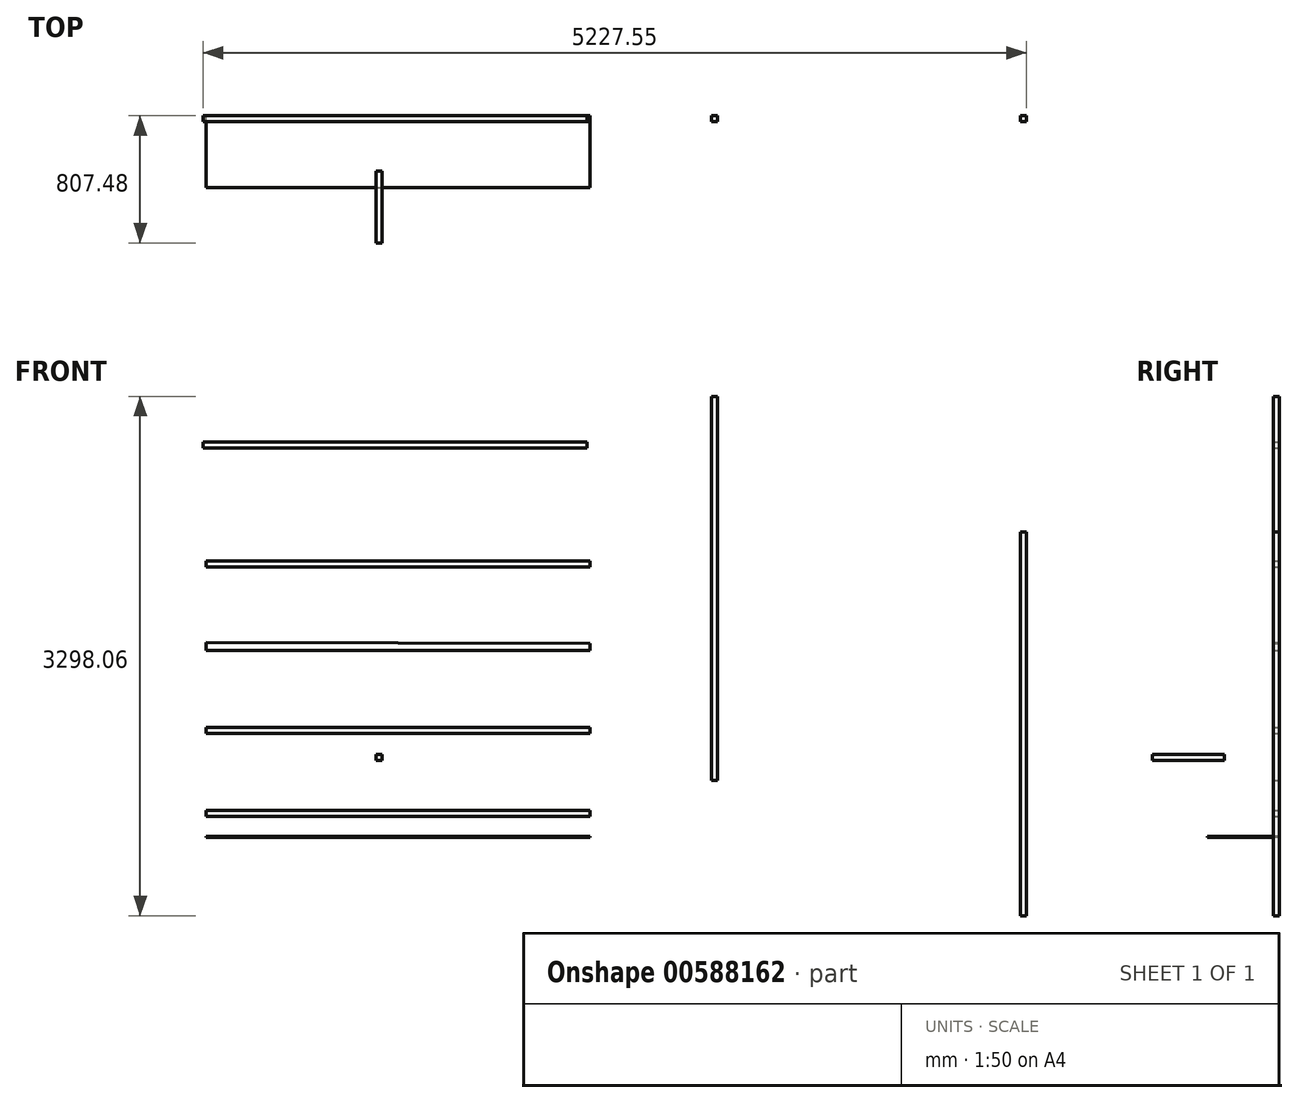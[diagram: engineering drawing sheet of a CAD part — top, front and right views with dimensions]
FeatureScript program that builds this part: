
annotation { "Feature Type Name" : "Feature", "Feature Type Description" : "" }
export const myFeature = defineFeature(function(context is Context, id is Id, definition is map)
    precondition{}
    {
        {
            var Q0;
            Q0=qCreatedBy(makeId("Front.planeOp"),FACE);
            var sketch = newSketch(context, id + "F0", { "sketchPlane" : qUnion([Q0])});
            skLineSegment(sketch, "E0", {"start": v(1359.2, 725.07) * mm, "end": v(1359.2, -1713.33) * mm});
            skLineSegment(sketch, "E1", {"start": v(-1079.2, 725.07) * mm, "end": v(-1079.2, -1713.33) * mm});
            skLineSegment(sketch, "E2", {"start": v(-1079.2, -525.88) * mm, "end": v(1359.2, -525.88) * mm});
            skLineSegment(sketch, "E3", {"start": v(-1079.2, -1052.93) * mm, "end": v(1359.2, -1052.93) * mm});
            skLineSegment(sketch, "E4.bottom", {"start": v(-1097.28, 798.65) * mm, "end": v(1341.12, 798.65) * mm});
            skLineSegment(sketch, "E4.top", {"start": v(-1097.28, 760.55) * mm, "end": v(1341.12, 760.55) * mm});
            skLineSegment(sketch, "E4.left", {"start": v(-1097.28, 798.65) * mm, "end": v(-1097.28, 760.55) * mm});
            skLineSegment(sketch, "E4.right", {"start": v(1341.12, 798.65) * mm, "end": v(1341.12, 760.55) * mm});
            skLineSegment(sketch, "E5.bottom", {"start": v(2131.45, 1087.28) * mm, "end": v(2169.55, 1087.28) * mm});
            skLineSegment(sketch, "E5.top", {"start": v(2131.45, -1351.12) * mm, "end": v(2169.55, -1351.12) * mm});
            skLineSegment(sketch, "E5.left", {"start": v(2131.45, 1087.28) * mm, "end": v(2131.45, -1351.12) * mm});
            skLineSegment(sketch, "E5.right", {"start": v(2169.55, 1087.28) * mm, "end": v(2169.55, -1351.12) * mm});
            skLineSegment(sketch, "E6", {"start": v(-1079.2, -1713.33) * mm, "end": v(1359.2, -1713.33) * mm});
            skLineSegment(sketch, "E7", {"start": v(-1079.2, -1579.98) * mm, "end": v(1359.2, -1579.98) * mm});
            skLineSegment(sketch, "E8", {"start": v(-1079.2, -1541.88) * mm, "end": v(1359.2, -1541.88) * mm});
            skLineSegment(sketch, "E9", {"start": v(-1079.64, -1014.83) * mm, "end": v(1359.2, -1014.83) * mm});
            skLineSegment(sketch, "E10", {"start": v(-1079.2, -475.58) * mm, "end": v(1359.2, -481.43) * mm});
            skLineSegment(sketch, "E11", {"start": v(-1079.2, 3.19) * mm, "end": v(1359.2, 3.19) * mm});
            skLineSegment(sketch, "E12", {"start": v(-1079.2, -1579.98) * mm, "end": v(-1079.2, -1541.88) * mm});
            skLineSegment(sketch, "E13", {"start": v(1359.2, -1014.83) * mm, "end": v(1359.2, -1052.93) * mm});
            skLineSegment(sketch, "E14", {"start": v(-1079.64, -1014.83) * mm, "end": v(-1079.2, -1052.93) * mm});
            skLineSegment(sketch, "E15", {"start": v(-1079.2, -475.58) * mm, "end": v(-1079.2, -525.88) * mm});
            skLineSegment(sketch, "E16", {"start": v(1359.2, -481.43) * mm, "end": v(1359.2, -525.88) * mm});
            skLineSegment(sketch, "E17", {"start": v(1359.2, 41.29) * mm, "end": v(-1079.2, 41.29) * mm});
            skLineSegment(sketch, "E18", {"start": v(-1079.2, 41.29) * mm, "end": v(-1079.2, 13.37) * mm});
            skLineSegment(sketch, "E19", {"start": v(1359.2, 41.29) * mm, "end": v(1359.2, 7.02) * mm});
            skLineSegment(sketch, "E20.bottom", {"start": v(4092.17, 227.62) * mm, "end": v(4130.27, 227.62) * mm});
            skLineSegment(sketch, "E20.top", {"start": v(4092.17, -2210.78) * mm, "end": v(4130.27, -2210.78) * mm});
            skLineSegment(sketch, "E20.left", {"start": v(4092.17, 227.62) * mm, "end": v(4092.17, -2210.78) * mm});
            skLineSegment(sketch, "E20.right", {"start": v(4130.27, 227.62) * mm, "end": v(4130.27, -2210.78) * mm});
            skSolve(sketch);
        }
        {
            var Q0;
            Q0=makeQuery(id+"F0.imprint","IMPRINT",FACE,{"disambiguationData":[TD([[makeQuery(id+"F0.imprint","IMPRINT",EDGE,{"derivedFrom":sQuery(id+"F0.wireOp",EDGE,"E4.bottom")}),-1.0]])]});
            extrude(context, id + "F1", {"entities" : qUnion([Q0]), "depth" : 38.1 * mm, "offsetDistance" : 25.4 * mm});
        }
        {
            var Q0;
            Q0=makeQuery(id+"F0.imprint","IMPRINT",FACE,{"disambiguationData":[TD([[makeQuery(id+"F0.imprint","IMPRINT",EDGE,{"derivedFrom":sQuery(id+"F0.wireOp",EDGE,"E5.bottom")}),-1.0]])]});
            extrude(context, id + "F2", {"entities" : qUnion([Q0]), "depth" : 38.1 * mm, "offsetDistance" : 25.4 * mm});
        }
        {
            var Q0;
            {var subQ0=sQuery(id+"F0.wireOp",EDGE,"E7");Q0=makeQuery(id+"F0.imprint","IMPRINT",FACE,{"disambiguationData":[TD([[makeQuery(id+"F0.imprint","IMPRINT",EDGE,{"derivedFrom":subQ0}),1.0]])]});}
            extrude(context, id + "F3", {"entities" : qUnion([Q0]), "depth" : 38.1 * mm, "offsetDistance" : 25.4 * mm});
        }
        {
            var Q0;
            {var subQ0=sQuery(id+"F0.wireOp",EDGE,"E3");Q0=makeQuery(id+"F0.imprint","IMPRINT",FACE,{"disambiguationData":[TD([[makeQuery(id+"F0.imprint","IMPRINT",EDGE,{"derivedFrom":subQ0}),1.0]])]});}
            extrude(context, id + "F4", {"entities" : qUnion([Q0]), "depth" : 38.1 * mm, "offsetDistance" : 25.4 * mm});
        }
        {
            var Q0;
            Q0=makeQuery(id+"F0.imprint","IMPRINT",FACE,{"disambiguationData":[TD([[makeQuery(id+"F0.imprint","IMPRINT",EDGE,{"derivedFrom":sQuery(id+"F0.wireOp",EDGE,"E11")}),1.0]])]});
            extrude(context, id + "F5", {"entities" : qUnion([Q0]), "depth" : 38.1 * mm, "offsetDistance" : 25.4 * mm});
        }
        {
            var Q0;
            Q0=makeQuery(id+"F0.imprint","IMPRINT",FACE,{"disambiguationData":[TD([[makeQuery(id+"F0.imprint","IMPRINT",EDGE,{"derivedFrom":sQuery(id+"F0.wireOp",EDGE,"E2")}),1.0]])]});
            extrude(context, id + "F6", {"entities" : qUnion([Q0]), "depth" : 38.1 * mm, "offsetDistance" : 25.4 * mm});
        }
        {
            var Q0;
            Q0=sQuery(id+"F0.wireOp",EDGE,"E6");
            extrude(context, id + "F7", {"bodyType" : ToolBodyType.SURFACE, "surfaceEntities" : qUnion([Q0]), "depth" : 457.2 * mm, "offsetDistance" : 25.4 * mm});
        }
        {
            var Q0;
            Q0=makeQuery(id+"F7.opExtrude","SWEPT_FACE",FACE,{"disambiguationData":[OSD([sQuery(id+"F0.wireOp",EDGE,"E6")])]});
            extrude(context, id + "F8", {"entities" : qUnion([Q0]), "oppositeDirection" : true, "depth" : 6.35 * mm, "offsetDistance" : 25.4 * mm});
        }
        {
            var Q0;
            Q0=makeQuery(id+"F0.imprint","IMPRINT",FACE,{"disambiguationData":[TD([[makeQuery(id+"F0.imprint","IMPRINT",EDGE,{"derivedFrom":sQuery(id+"F0.wireOp",EDGE,"E20.bottom")}),-1.0]])]});
            var Q1;
            Q1=sQuery(id+"F0.wireOp",EDGE,"E20.right");
            extrude(context, id + "F9", {"entities" : qUnion([Q0]), "surfaceEntities" : qUnion([Q1]), "depth" : 38.1 * mm, "offsetDistance" : 25.4 * mm});
        }
        {
            var Q0;
            Q0=qCreatedBy(makeId("Right.planeOp"),FACE);
            var sketch = newSketch(context, id + "F10", { "sketchPlane" : qUnion([Q0])});
            skLineSegment(sketch, "E21.bottom", {"start": v(-807.48, -1223.73) * mm, "end": v(-350.28, -1223.73) * mm});
            skLineSegment(sketch, "E21.top", {"start": v(-807.48, -1185.63) * mm, "end": v(-350.28, -1185.63) * mm});
            skLineSegment(sketch, "E21.left", {"start": v(-807.48, -1223.73) * mm, "end": v(-807.48, -1185.63) * mm});
            skLineSegment(sketch, "E21.right", {"start": v(-350.28, -1223.73) * mm, "end": v(-350.28, -1185.63) * mm});
            skSolve(sketch);
        }
        {
            var Q0;
            Q0=makeQuery(id+"F10.imprint","IMPRINT",FACE,{"disambiguationData":[TD([[makeQuery(id+"F10.imprint","IMPRINT",EDGE,{"derivedFrom":sQuery(id+"F10.wireOp",EDGE,"E21.bottom")}),1.0]])]});
            extrude(context, id + "F11", {"entities" : qUnion([Q0]), "depth" : 38.1 * mm, "offsetDistance" : 25.4 * mm});
        }
    });
